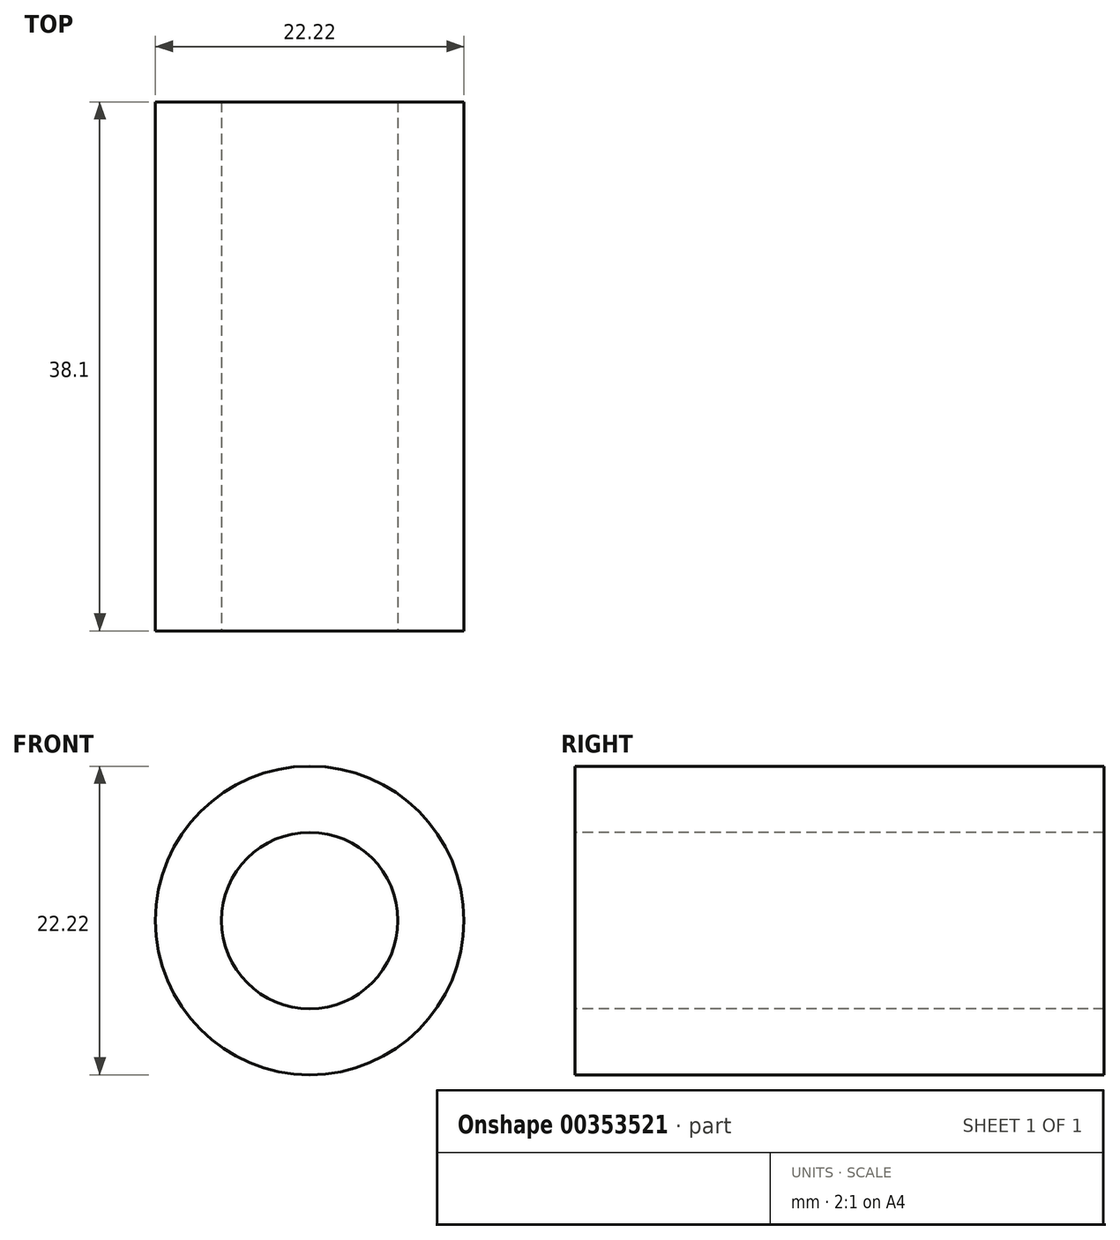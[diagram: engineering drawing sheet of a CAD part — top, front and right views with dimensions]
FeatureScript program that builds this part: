
annotation { "Feature Type Name" : "Feature", "Feature Type Description" : "" }
export const myFeature = defineFeature(function(context is Context, id is Id, definition is map)
    precondition{}
    {
        {
            var Q0;
            Q0=qCreatedBy(makeId("Front.planeOp"),FACE);
            var sketch = newSketch(context, id + "F0", { "sketchPlane" : qUnion([Q0])});
            skCircle(sketch, "E0", {"center": v(0, 0) * mm, "radius": 11.11 * mm});
            skSolve(sketch);
        }
        {
            var Q0;
            Q0=qSketchRegion(id+"F0",true);
            extrude(context, id + "F1", {"entities" : qUnion([Q0]), "depth" : 38.1 * mm, "symmetric" : true});
        }
        {
            var Q0;
            Q0=makeQuery(id+"F1.opExtrude","CAP_FACE",FACE,{"disambiguationData":[OSD([sQuery(id+"F0.wireOp",EDGE,"E0")])],"isStart":false});
            var sketch = newSketch(context, id + "F2", { "sketchPlane" : qUnion([Q0])});
            skCircle(sketch, "E1", {"center": v(0, 0) * mm, "radius": 6.35 * mm});
            skSolve(sketch);
        }
        {
            var Q0;
            Q0=qSketchRegion(id+"F2",true);
            extrude(context, id + "F3", {"entities" : qUnion([Q0]), "operationType" : NewBodyOperationType.REMOVE, "oppositeDirection" : true, "depth" : 88.9 * mm});
        }
    });
